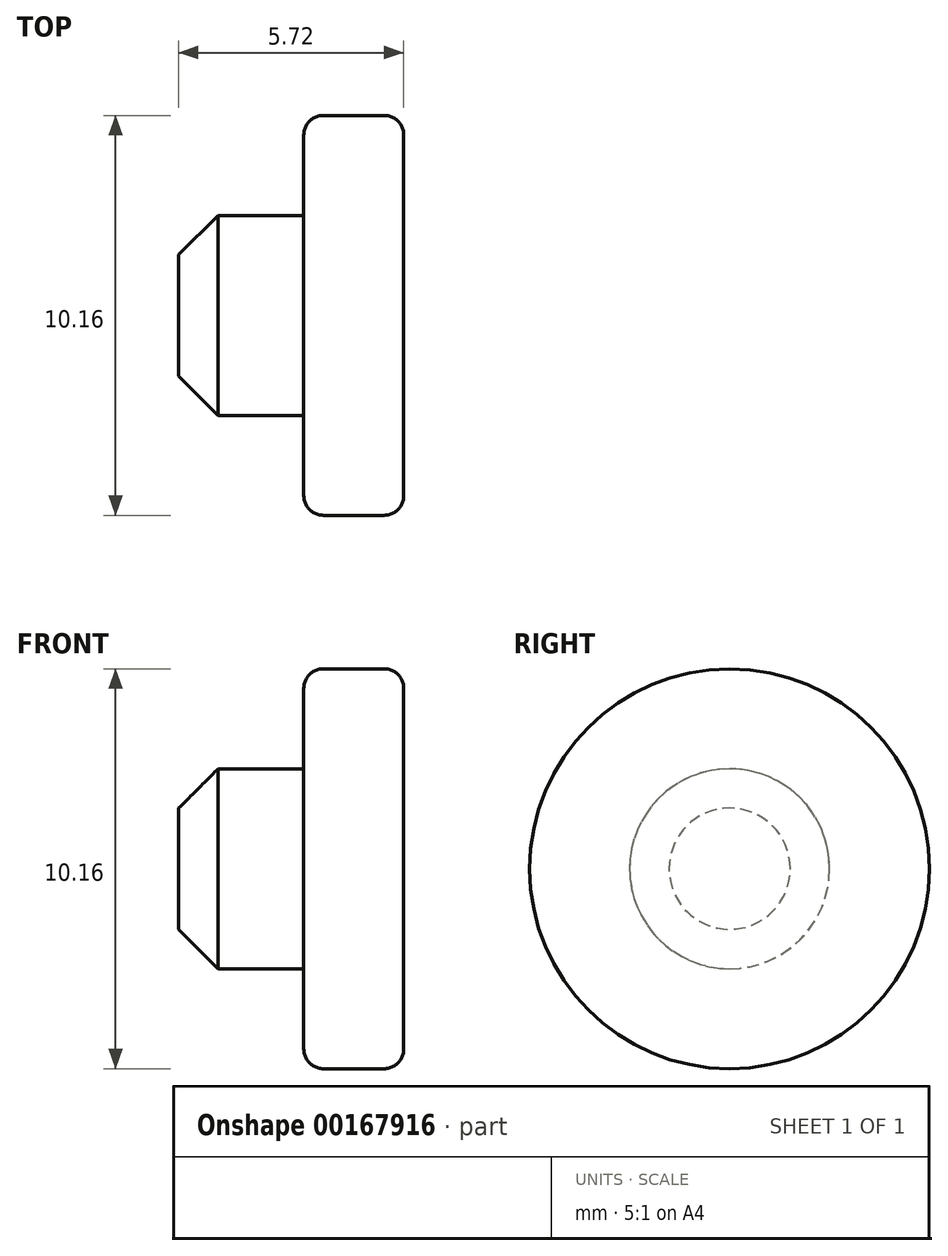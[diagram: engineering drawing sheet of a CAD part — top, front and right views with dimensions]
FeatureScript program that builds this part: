
annotation { "Feature Type Name" : "Feature", "Feature Type Description" : "" }
export const myFeature = defineFeature(function(context is Context, id is Id, definition is map)
    precondition{}
    {
        {
            var Q0;
            Q0=qCreatedBy(makeId("Front.planeOp"),FACE);
            var sketch = newSketch(context, id + "F0", { "sketchPlane" : qUnion([Q0])});
            skLineSegment(sketch, "E0", {"start": v(0, 2.54) * mm, "end": v(0, 5.08) * mm});
            skLineSegment(sketch, "E1", {"start": v(0, 5.08) * mm, "end": v(2.54, 5.08) * mm});
            skLineSegment(sketch, "E2", {"start": v(0, 2.54) * mm, "end": v(-3.17, 2.54) * mm});
            skLineSegment(sketch, "E3", {"start": v(-3.17, 2.54) * mm, "end": v(-3.17, 0) * mm});
            skLineSegment(sketch, "E4", {"start": v(-3.18, 0) * mm, "end": v(-45.57, 0) * mm, "construction": true});
            skLineSegment(sketch, "E5", {"start": v(2.54, 5.08) * mm, "end": v(2.54, 0) * mm});
            skLineSegment(sketch, "E6", {"start": v(-3.17, 0) * mm, "end": v(2.54, 0) * mm});
            skSolve(sketch);
        }
        {
            var Q0;
            Q0=makeQuery(id+"F0.imprint","IMPRINT",FACE,{"disambiguationData":[TD([[makeQuery(id+"F0.imprint","IMPRINT",EDGE,{"derivedFrom":sQuery(id+"F0.wireOp",EDGE,"E0")}),-1.0]])]});
            var Q1;
            Q1=sQuery(id+"F0.wireOp",EDGE,"E4");
            revolve(context, id + "F1", {"entities" : qUnion([Q0]), "axis" : qUnion([Q1]), "revolveType" : RevolveType.FULL});
        }
        {
            var Q0;
            Q0=makeQuery(id+"F1.opRevolve","SWEPT_EDGE",EDGE,{"disambiguationData":[OSD([sQuery(id+"F0.wireOp",EDGE,"E2"),sQuery(id+"F0.wireOp",EDGE,"E3")])]});
            chamfer(context, id + "F2", {"entities" : qUnion([Q0]), "width" : 1 * mm, "tangentPropagation" : true});
        }
        {
            var Q0;
            Q0=makeQuery(id+"F1.opRevolve","SWEPT_EDGE",EDGE,{"disambiguationData":[OSD([sQuery(id+"F0.wireOp",EDGE,"E1"),sQuery(id+"F0.wireOp",EDGE,"f116393f-260c-4282-ae79-4cf0828432b6")])]});
            fillet(context, id + "F3", {"entities" : qUnion([Q0]), "radius" : .5 * mm, "tangentPropagation" : true, "allowEdgeOverflow" : false});
        }
    });
